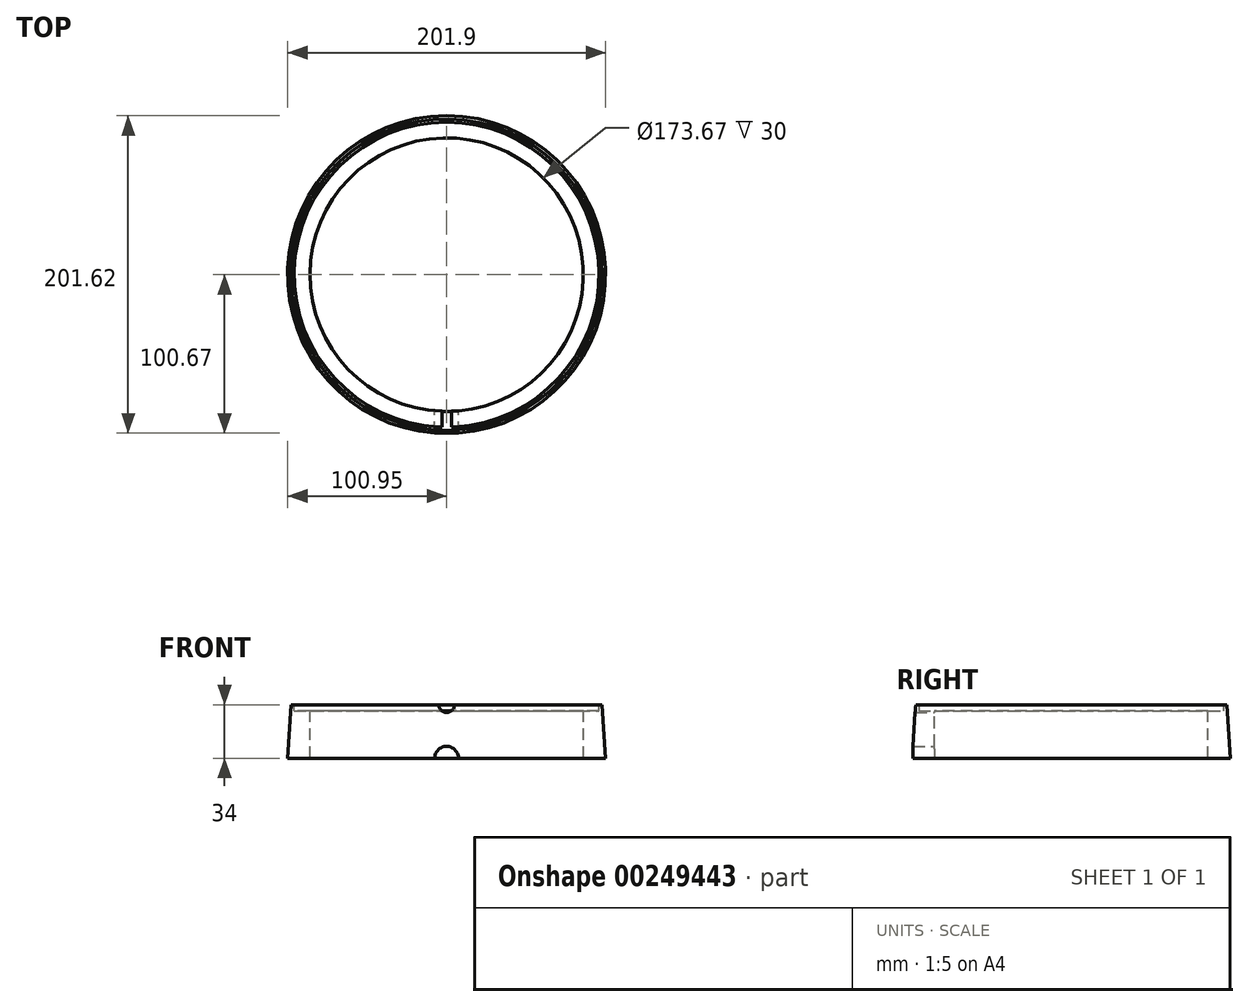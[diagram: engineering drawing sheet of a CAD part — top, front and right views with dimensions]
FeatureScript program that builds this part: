
annotation { "Feature Type Name" : "Feature", "Feature Type Description" : "" }
export const myFeature = defineFeature(function(context is Context, id is Id, definition is map)
    precondition{}
    {
        {
            var Q0;
            Q0=qCreatedBy(makeId("Front.planeOp"),FACE);
            var sketch = newSketch(context, id + "F0", { "sketchPlane" : qUnion([Q0])});
            skLineSegment(sketch, "E0", {"start": v(0, 71.6) * mm, "end": v(0, -81.32) * mm, "construction": true});
            skLineSegment(sketch, "E1", {"start": v(0, 0) * mm, "end": v(-96.84, 0) * mm, "construction": true});
            skLineSegment(sketch, "E2.MirrorCS", {"start": v(0, 0) * mm, "end": v(96.84, 0) * mm, "construction": true});
            skLineSegment(sketch, "E3", {"start": v(-96.84, 30) * mm, "end": v(-86.84, 30) * mm});
            skLineSegment(sketch, "E4", {"start": v(-86.84, 30) * mm, "end": v(-86.84, 0) * mm});
            skLineSegment(sketch, "E5", {"start": v(-86.84, 0) * mm, "end": v(-96.84, 0) * mm});
            skLineSegment(sketch, "E6", {"start": v(-96.84, 30) * mm, "end": v(-96.84, 34) * mm});
            skLineSegment(sketch, "E7", {"start": v(-96.84, 34) * mm, "end": v(-98.84, 34) * mm});
            skLineSegment(sketch, "E8", {"start": v(-98.84, 34) * mm, "end": v(-100.95, 0) * mm});
            skLineSegment(sketch, "E9", {"start": v(-96.84, 0) * mm, "end": v(-100.95, 0) * mm});
            skLineSegment(sketch, "E10", {"start": v(-96.84, 30) * mm, "end": v(-96.84, 0) * mm, "construction": true});
            skSolve(sketch);
        }
        {
            var Q0;
            Q0=makeQuery(id+"F0.imprint","IMPRINT",FACE,{"disambiguationData":[TD([[makeQuery(id+"F0.imprint","IMPRINT",EDGE,{"derivedFrom":sQuery(id+"F0.wireOp",EDGE,"E3")}),-1.0]])]});
            var Q1;
            Q1=sQuery(id+"F0.wireOp",EDGE,"E0");
            revolve(context, id + "F1", {"entities" : qUnion([Q0]), "axis" : qUnion([Q1]), "revolveType" : RevolveType.FULL});
        }
        {
            var Q0;
            Q0=qCreatedBy(makeId("Front.planeOp"),FACE);
            var sketch = newSketch(context, id + "F2", { "sketchPlane" : qUnion([Q0])});
            skLineSegment(sketch, "E11", {"start": v(0, 0) * mm, "end": v(-3, 0) * mm});
            skLineSegment(sketch, "E12.MirrorCS", {"start": v(0, 0) * mm, "end": v(3, 0) * mm});
            skLineSegment(sketch, "E13.0", {"start": v(-98.84, 34) * mm, "end": v(98.84, 34) * mm});
            skArc(sketch, "E14", {"start": v(-5, 34) * mm, "mid": v(0, 29) * mm, "end": v(5, 34) * mm});
            skSolve(sketch);
        }
        {
            var Q0;
            Q0=qCreatedBy(makeId("Front.planeOp"),FACE);
            var sketch = newSketch(context, id + "F3", { "sketchPlane" : qUnion([Q0])});
            skArc(sketch, "E15", {"start": v(7.5, 0) * mm, "mid": v(0, 7.5) * mm, "end": v(-7.5, 0) * mm});
            skLineSegment(sketch, "E16.0", {"start": v(0, 0) * mm, "end": v(-96.84, 0) * mm});
            skLineSegment(sketch, "E17.0", {"start": v(0, 0) * mm, "end": v(96.84, 0) * mm});
            skSolve(sketch);
        }
        {
            var Q0;
            {var subQ0=sQuery(id+"F2.wireOp",EDGE,"E14");Q0=makeQuery(id+"F2.imprint","IMPRINT",FACE,{"disambiguationData":[TD([[makeQuery(id+"F2.imprint","IMPRINT",EDGE,{"derivedFrom":subQ0}),1.0]])]});}
            var Q1;
            {var subQ0=sQuery(id+"F3.wireOp",EDGE,"E15");Q1=makeQuery(id+"F3.imprint","IMPRINT",FACE,{"disambiguationData":[TD([[makeQuery(id+"F3.imprint","IMPRINT",EDGE,{"derivedFrom":subQ0}),1.0]])]});}
            extrude(context, id + "F4", {"entities" : qUnion([Q0, Q1]), "operationType" : NewBodyOperationType.REMOVE, "depth" : 122.3 * mm});
        }
    });
